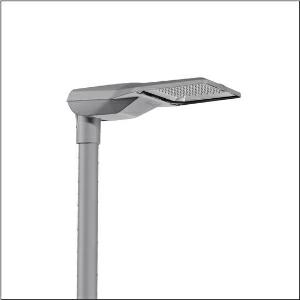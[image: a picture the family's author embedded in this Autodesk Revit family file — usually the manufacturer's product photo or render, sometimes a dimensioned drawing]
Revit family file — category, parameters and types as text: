
# Revit family: streetlight_sl_21_iq_midi___pl52_5xe3h31d08mb_2c0b
name_source: partatom
category: Lighting Fixtures
units: mm (PartAtom-declared; Revit-internal decimal feet)

## family parameters
Cut with Voids When Loaded = No
Host = Face
Light Source = No
Part Type = Normal
Room Calculation Point = No
Round Connector Dimension = Use Diameter
Shared = No

## types (1)
- --- (1 x LED, 19170 lm, 146.7 W, 3000K)
    Apparent Load = 147 VA
    CIE Flux Codes = 27 59 98 100 100
    Color Rendering = 70
    Color Temperature = 3000K
    Default Elevation = 1800 mm
    Description = Streetlight SL 21 iQ midi, mast luminaire, primary light control with lens, of PMMA, primary optical cover: cover, of toughened safety glass, transparent, light distribution: PL52, light emission: direct distribution, primary light characteristic: asymmetric, installation type: post-top, side-entry, LED, High Power LED, rated luminous flux: 19.170lm, luminous efficacy: 131lm/W, light colour: 730, colour temperature: 3000K, control: Auto-Match, Temp-Guard, Lumen-Switch, Night-Set, Smart-Wire, Light-Fading, Desk-Remote (wireless, voltage-free reading and setting of iQ features in the workshop via application-optimized NFC function/RFID function), optimised constant luminous flux control (CLO 2.0), presetting dimming linear, mains connection: 230..240V, AC, 50/60Hz, start of lifetime: 147W, end of service life: 161W, reduction: 62W, luminaire housing, of diecast aluminium, powder-coated, Siteco® metallic grey (DB 702S), corrosivity category C5 mid according to DIN EN ISO 12944, please order mast flange separately, inclination adjustable: 0°, 5°, 10°, 15°, sealing non-destructively replaceable, multi-level sealing system, length: 644mm, width: 335mm, height: 110mm, mast flange for spigot size: 42mm (side-entry): 5XC10008XM4, 60/48mm (side-entry/post-top): 5XC10108XM2, 76/60mm (side-entry/post-top): 5XC10108XM1, protection rating (complete): IP66, insulation class (complete): insulation class II (safety insulation), certification: CE, ENEC, ENEC+, VDE, impact resistance: IK09, permissible operating ambient temperature for outdoor applications: -40..+50°C, standard-compliant lighting for roads and squares, packaging unit: 1 piece

Light Distribution: PL52
    Height = 111 mm
    Lamp = 1 x LED
    Lamp Light Flux = 19170 lm
    Lamp Power = 146.7 W
    Lamp count = 1
    Length = 644 mm
    Luminous efficacy = 131 lm/W
    Manufacturer = Siteco
    ModVariant = No
    Model = 5XE3H31D08MB
    Number of Poles = 1
    OnlyDefault = Yes
    Power Factor = 1
    Product Name = Streetlight SL 21 iQ midi | PL52
    Product group = mast luminaire | pylon top
    ProductGroupID = 6100
    Protection Class = Protection class II
    Protection Degree = IP 66
    RLX_Detail_Level = 1
    RLX_Emergency_Light_Flux = 0 lm
    RLX_Emergency_Type = 0
    RLX_Emergency_Type_DB = No
    RlxData = <blob elided: 100017 chars, md5=f9c40444>
    Socket = socket
    Standby Power = 0 W
    System Light Flux = 19169 lm
    System Power = 147 W
    Type Comments = factory setting: luminous flux: 100 % | dim-lin: 254 | 753 mA
    Type Image = l_1004298.jpg
    URL = http://relux.com
    VarID = @adj_143293
    Voltage = 0 V
    Weight = 0.00 kg
    Width = 336 mm

## geometry (parser evidence)
native form markers: Blend x4, Sweep x10
no freeform markers — native parametric forms only
